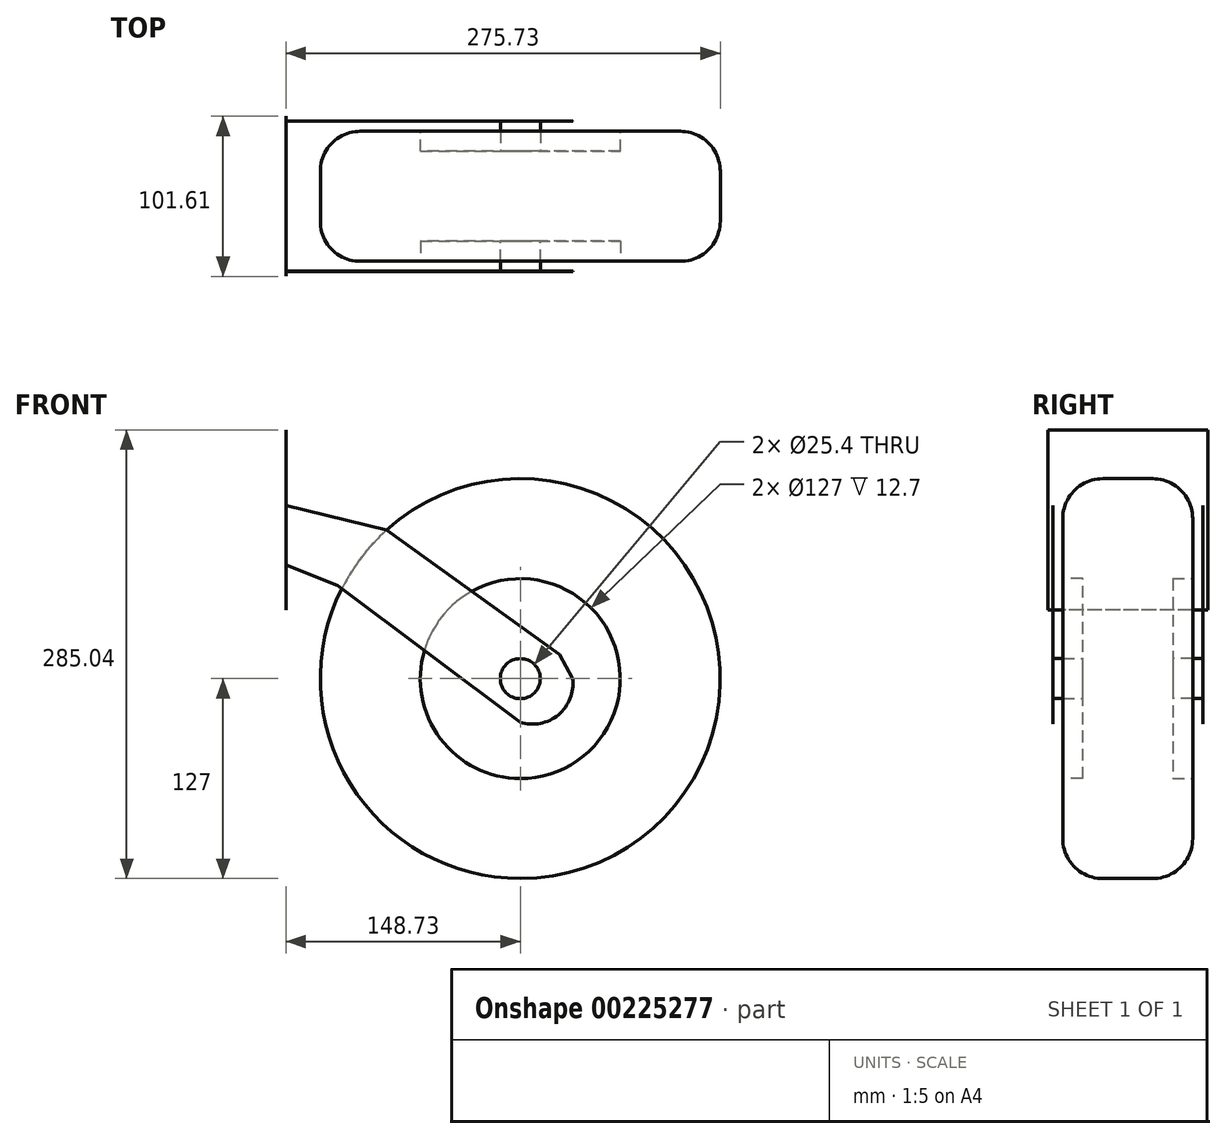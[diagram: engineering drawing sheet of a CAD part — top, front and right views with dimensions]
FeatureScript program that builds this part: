
annotation { "Feature Type Name" : "Feature", "Feature Type Description" : "" }
export const myFeature = defineFeature(function(context is Context, id is Id, definition is map)
    precondition{}
    {
        {
            var Q0;
            Q0=qCreatedBy(makeId("Front.planeOp"),FACE);
            var sketch = newSketch(context, id + "F0", { "sketchPlane" : qUnion([Q0])});
            skCircle(sketch, "E0", {"center": v(0, 0) * mm, "radius": 127 * mm});
            skSolve(sketch);
        }
        {
            var Q0;
            Q0=makeQuery(id+"F0.imprint","IMPRINT",FACE,{"disambiguationData":[TD([[makeQuery(id+"F0.imprint","IMPRINT",EDGE,{"derivedFrom":sQuery(id+"F0.wireOp",EDGE,"E0")}),1.0]])]});
            extrude(context, id + "F1", {"entities" : qUnion([Q0]), "depth" : 82.55 * mm});
        }
        {
            var Q0;
            Q0=makeQuery(id+"F1.opExtrude","CAP_EDGE",EDGE,{"disambiguationData":[OSD([sQuery(id+"F0.wireOp",EDGE,"E0")])],"isStart":true});
            var Q1;
            Q1=makeQuery(id+"F1.opExtrude","CAP_EDGE",EDGE,{"disambiguationData":[OSD([sQuery(id+"F0.wireOp",EDGE,"E0")])],"isStart":false});
            fillet(context, id + "F2", {"entities" : qUnion([Q0, Q1]), "radius" : 25.4 * mm, "tangentPropagation" : true, "allowEdgeOverflow" : false});
        }
        {
            var Q0;
            Q0=makeQuery(id+"F1.opExtrude","CAP_FACE",FACE,{"disambiguationData":[OSD([sQuery(id+"F0.wireOp",EDGE,"E0")])],"isStart":false});
            var sketch = newSketch(context, id + "F3", { "sketchPlane" : qUnion([Q0])});
            skCircle(sketch, "E1", {"center": v(0, 0) * mm, "radius": 63.5 * mm});
            skSolve(sketch);
        }
        {
            var Q0;
            Q0=makeQuery(id+"F3.imprint","IMPRINT",FACE,{"disambiguationData":[TD([[makeQuery(id+"F3.imprint","IMPRINT",EDGE,{"derivedFrom":sQuery(id+"F3.wireOp",EDGE,"E1")}),1.0]])]});
            extrude(context, id + "F4", {"entities" : qUnion([Q0]), "operationType" : NewBodyOperationType.REMOVE, "oppositeDirection" : true, "depth" : 12.7 * mm});
        }
        {
            var Q0;
            Q0=makeQuery(id+"F1.opExtrude","CAP_FACE",FACE,{"disambiguationData":[OSD([sQuery(id+"F0.wireOp",EDGE,"E0")])],"isStart":true});
            var sketch = newSketch(context, id + "F5", { "sketchPlane" : qUnion([Q0])});
            skCircle(sketch, "E2", {"center": v(0, 0) * mm, "radius": 63.5 * mm});
            skSolve(sketch);
        }
        {
            var Q0;
            Q0=makeQuery(id+"F1.opExtrude","CAP_FACE",FACE,{"disambiguationData":[OSD([sQuery(id+"F0.wireOp",EDGE,"E0")])],"isStart":false});
            cPlane(context, id + "F6", {"entities" : qUnion([Q0]), "cplaneType" : CPlaneType.OFFSET, "offset" : 41.27 * mm, "oppositeDirection" : true, "width" : 152.4 * mm, "height" : 152.4 * mm});
        }
        {
            var Q0;
            Q0=makeQuery(id+"F5.imprint","IMPRINT",FACE,{"disambiguationData":[TD([[makeQuery(id+"F5.imprint","IMPRINT",EDGE,{"derivedFrom":sQuery(id+"F5.wireOp",EDGE,"E2")}),1.0]])]});
            extrude(context, id + "F7", {"entities" : qUnion([Q0]), "operationType" : NewBodyOperationType.REMOVE, "oppositeDirection" : true, "depth" : 12.7 * mm});
        }
        {
            var Q0;
            Q0=makeQuery(id+"F7.boolean.opBoolean","COPY",FACE,{"derivedFrom":makeQuery(id+"F7.opExtrude","CAP_FACE",FACE,{"disambiguationData":[OSD([sQuery(id+"F5.wireOp",EDGE,"E2")])],"isStart":false})});
            var sketch = newSketch(context, id + "F8", { "sketchPlane" : qUnion([Q0])});
            skCircle(sketch, "E3", {"center": v(0, 0) * mm, "radius": 12.7 * mm});
            skSolve(sketch);
        }
        {
            var Q0;
            Q0=makeQuery(id+"F8.imprint","IMPRINT",FACE,{"disambiguationData":[TD([[makeQuery(id+"F8.imprint","IMPRINT",EDGE,{"derivedFrom":sQuery(id+"F8.wireOp",EDGE,"E3")}),1.0]])]});
            extrude(context, id + "F9", {"entities" : qUnion([Q0]), "operationType" : NewBodyOperationType.ADD, "depth" : 19.05 * mm});
        }
        {
            var Q0;
            Q0=makeQuery(id+"F4.boolean.opBoolean","COPY",FACE,{"derivedFrom":makeQuery(id+"F4.opExtrude","CAP_FACE",FACE,{"disambiguationData":[OSD([sQuery(id+"F3.wireOp",EDGE,"E1")])],"isStart":false})});
            var sketch = newSketch(context, id + "F10", { "sketchPlane" : qUnion([Q0])});
            skCircle(sketch, "E4", {"center": v(0, 0) * mm, "radius": 12.7 * mm});
            skSolve(sketch);
        }
        {
            var Q0;
            Q0=makeQuery(id+"F10.imprint","IMPRINT",FACE,{"disambiguationData":[TD([[makeQuery(id+"F10.imprint","IMPRINT",EDGE,{"derivedFrom":sQuery(id+"F10.wireOp",EDGE,"E4")}),1.0]])]});
            extrude(context, id + "F11", {"entities" : qUnion([Q0]), "operationType" : NewBodyOperationType.ADD, "depth" : 19.05 * mm});
        }
        {
            var Q0;
            Q0=makeQuery(id+"F11.opExtrude","CAP_FACE",FACE,{"disambiguationData":[OSD([sQuery(id+"F10.wireOp",EDGE,"E4")])],"isStart":false});
            var sketch = newSketch(context, id + "F12", { "sketchPlane" : qUnion([Q0])});
            skLineSegment(sketch, "E5", {"start": v(0, -27.77) * mm, "end": v(-116.14, 59.08) * mm});
            skLineSegment(sketch, "E6", {"start": v(-116.14, 59.08) * mm, "end": v(-148.72, 72.07) * mm});
            skLineSegment(sketch, "E7", {"start": v(-148.72, 72.07) * mm, "end": v(-148.72, 110.03) * mm});
            skLineSegment(sketch, "E8", {"start": v(-148.72, 110.03) * mm, "end": v(-84.94, 94.3) * mm});
            skLineSegment(sketch, "E9", {"start": v(-84.94, 94.3) * mm, "end": v(24.87, 15.5) * mm});
            skLineSegment(sketch, "E10", {"start": v(24.87, 15.5) * mm, "end": v(33.26, 0) * mm});
            skArc(sketch, "E11", {"start": v(0, -27.77) * mm, "mid": v(24.18, -22.93) * mm, "end": v(33.26, 0) * mm});
            skSolve(sketch);
        }
        {
            var Q0;
            Q0=makeQuery(id+"F12.imprint","IMPRINT",FACE,{"disambiguationData":[TD([[makeQuery(id+"F12.imprint","IMPRINT",EDGE,{"derivedFrom":sQuery(id+"F12.wireOp",EDGE,"E5")}),-1.0]])]});
            extrude(context, id + "F13", {"entities" : qUnion([Q0]), "depth" : 1 / 203.2 * mm});
        }
        {
            var Q0;
            Q0=makeQuery(id+"F13.opExtrude","SWEPT_BODY",BODY,{"disambiguationData":[OSD([sQuery(id+"F10.wireOp",EDGE,"E4"),sQuery(id+"F12.wireOp",EDGE,"E5"),sQuery(id+"F12.wireOp",EDGE,"E6"),sQuery(id+"F12.wireOp",EDGE,"E7"),sQuery(id+"F12.wireOp",EDGE,"E8"),sQuery(id+"F12.wireOp",EDGE,"E9"),sQuery(id+"F12.wireOp",EDGE,"E10"),sQuery(id+"F12.wireOp",EDGE,"E11")])]});
            var Q1;
            Q1=qCreatedBy(id+"F6.planeOp",FACE);
            mirror(context, id + "F14", {"entities" : qUnion([Q0]), "mirrorPlane" : qUnion([Q1])});
        }
        {
            var Q0;
            Q0=makeQuery(id+"F14.opPattern","COPY",FACE,{"derivedFrom":makeQuery(id+"F13.opExtrude","SWEPT_FACE",FACE,{"disambiguationData":[OSD([sQuery(id+"F12.wireOp",EDGE,"E7")])]}),"instanceName":"1"});
            var sketch = newSketch(context, id + "F15", { "sketchPlane" : qUnion([Q0])});
            skLineSegment(sketch, "E12.bottom", {"start": v(-9.52, 43.74) * mm, "end": v(92.08, 43.74) * mm});
            skLineSegment(sketch, "E12.top", {"start": v(-9.52, 158.04) * mm, "end": v(92.08, 158.04) * mm});
            skLineSegment(sketch, "E12.left", {"start": v(-9.52, 43.74) * mm, "end": v(-9.52, 158.04) * mm});
            skLineSegment(sketch, "E12.right", {"start": v(92.08, 43.74) * mm, "end": v(92.08, 158.04) * mm});
            skPoint(sketch, "E12.middle", {"position": v(41.28, 100.89) * mm});
            skSolve(sketch);
        }
        {
            var Q0;
            {var subQ5=sQuery(id+"F15.wireOp",EDGE,"E12.bottom");Q0=makeQuery(id+"F15.imprint","IMPRINT",FACE,{"disambiguationData":[TD([[makeQuery(id+"F15.imprint","IMPRINT",EDGE,{"derivedFrom":subQ5}),1.0]])]});}
            var Q1;
            {var subQ1=sQuery(id+"F12.wireOp",EDGE,"E7");Q1=makeQuery(id+"F15.imprint","IMPRINT",FACE,{"disambiguationData":[TD([[makeQuery(id+"F15.imprint","IMPRINT",EDGE,{"derivedFrom":makeQuery(id+"F14.opPattern","COPY",EDGE,{"derivedFrom":makeQuery(id+"F13.opExtrude","CAP_EDGE",EDGE,{"disambiguationData":[OSD([subQ1])],"isStart":true}),"instanceName":"1"})}),1.0]])]});}
            extrude(context, id + "F16", {"entities" : qUnion([Q0, Q1]), "operationType" : NewBodyOperationType.ADD, "depth" : 1 / 203.2 * mm});
        }
    });
